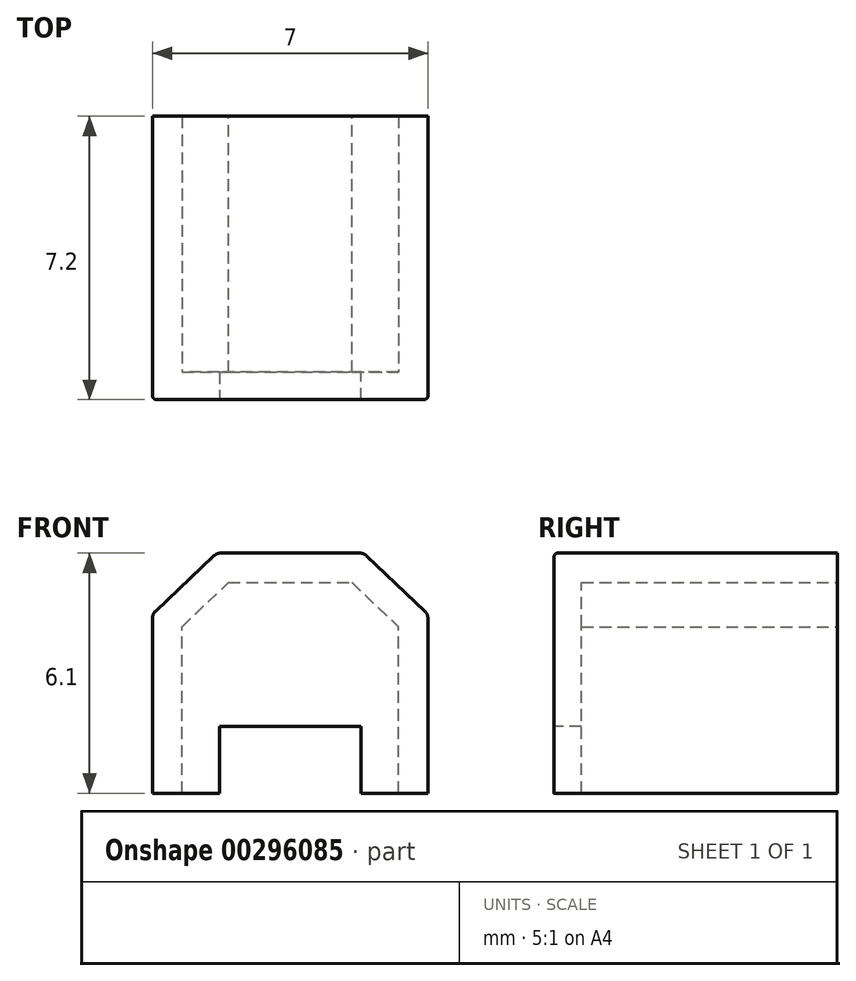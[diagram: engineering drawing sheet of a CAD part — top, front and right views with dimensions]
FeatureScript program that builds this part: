
annotation { "Feature Type Name" : "Feature", "Feature Type Description" : "" }
export const myFeature = defineFeature(function(context is Context, id is Id, definition is map)
    precondition{}
    {
        {
            var Q0;
            Q0=qCreatedBy(makeId("Front.planeOp"),FACE);
            var sketch = newSketch(context, id + "F0", { "sketchPlane" : qUnion([Q0])});
            skLineSegment(sketch, "E0.bottom", {"start": v(-3.5, 1.1) * mm, "end": v(3.5, 1.1) * mm});
            skLineSegment(sketch, "E0.left", {"start": v(-3.5, 1.1) * mm, "end": v(-3.5, 6.35) * mm});
            skLineSegment(sketch, "E0.right", {"start": v(3.5, 1.1) * mm, "end": v(3.5, 6.35) * mm});
            skPoint(sketch, "E1", {"position": v(0, 1.1) * mm});
            skLineSegment(sketch, "E2", {"start": v(-3.5, 6.35) * mm, "end": v(-1.87, 7.9) * mm});
            skLineSegment(sketch, "E3", {"start": v(-1.87, 7.9) * mm, "end": v(1.87, 7.9) * mm});
            skLineSegment(sketch, "E4", {"start": v(1.87, 7.9) * mm, "end": v(3.5, 6.35) * mm});
            skSolve(sketch);
        }
        {
            var Q0;
            Q0=makeQuery(id+"F0.imprint","IMPRINT",FACE,{"disambiguationData":[TD([[makeQuery(id+"F0.imprint","IMPRINT",EDGE,{"derivedFrom":sQuery(id+"F0.wireOp",EDGE,"E0.bottom")}),1.0]])]});
            extrude(context, id + "F1", {"entities" : qUnion([Q0]), "depth" : 7.2 * mm, "offsetDistance" : 25 * mm});
        }
        {
            var Q0;
            Q0=makeQuery(id+"F1.opExtrude","CAP_FACE",FACE,{"disambiguationData":[OSD([sQuery(id+"F0.wireOp",EDGE,"E0.bottom"),sQuery(id+"F0.wireOp",EDGE,"E0.left"),sQuery(id+"F0.wireOp",EDGE,"E0.right"),sQuery(id+"F0.wireOp",EDGE,"E2"),sQuery(id+"F0.wireOp",EDGE,"E3"),sQuery(id+"F0.wireOp",EDGE,"E4")])],"isStart":false});
            var sketch = newSketch(context, id + "F2", { "sketchPlane" : qUnion([Q0])});
            skLineSegment(sketch, "E5.0", {"start": v(-1.8, 1.1) * mm, "end": v(1.8, 1.1) * mm});
            skLineSegment(sketch, "E6", {"start": v(1.8, 1.1) * mm, "end": v(1.8, 3.5) * mm});
            skLineSegment(sketch, "E7", {"start": v(1.8, 3.5) * mm, "end": v(-1.8, 3.5) * mm});
            skLineSegment(sketch, "E8", {"start": v(-1.8, 3.5) * mm, "end": v(-1.8, 1.1) * mm});
            skPoint(sketch, "E9", {"position": v(0, 3.5) * mm});
            skPoint(sketch, "E10.orphan", {"position": v(-3.5, 1.1) * mm});
            skPoint(sketch, "E11.orphan", {"position": v(3.5, 1.1) * mm});
            skSolve(sketch);
        }
        {
            var Q0;
            Q0 = qSketchRegion(id + "F2", true);
            extrude(context, id + "F3", {"entities" : qUnion([Q0]), "operationType" : NewBodyOperationType.REMOVE, "endBound" : BoundingType.THROUGH_ALL, "oppositeDirection" : true, "depth" : 25 * mm, "offsetDistance" : 25 * mm});
        }
        {
            var Q0;
            Q0=makeQuery(id+"F1.opExtrude","CAP_FACE",FACE,{"disambiguationData":[OSD([sQuery(id+"F0.wireOp",EDGE,"E0.bottom"),sQuery(id+"F0.wireOp",EDGE,"E0.left"),sQuery(id+"F0.wireOp",EDGE,"E0.right"),sQuery(id+"F0.wireOp",EDGE,"E2"),sQuery(id+"F0.wireOp",EDGE,"E3"),sQuery(id+"F0.wireOp",EDGE,"E4")])],"isStart":true});
            var sketch = newSketch(context, id + "F4", { "sketchPlane" : qUnion([Q0])});
            skLineSegment(sketch, "E12.2", {"start": v(2.75, 1.1) * mm, "end": v(2.75, 6.03) * mm});
            skLineSegment(sketch, "E12.6", {"start": v(2.75, 6.03) * mm, "end": v(1.57, 7.15) * mm});
            skLineSegment(sketch, "E12.7", {"start": v(1.57, 7.15) * mm, "end": v(-1.57, 7.15) * mm});
            skLineSegment(sketch, "E12.8", {"start": v(-1.57, 7.15) * mm, "end": v(-2.75, 6.03) * mm});
            skLineSegment(sketch, "E12.9", {"start": v(-2.75, 1.1) * mm, "end": v(-2.75, 6.03) * mm});
            skLineSegment(sketch, "E13", {"start": v(-2.75, 1.1) * mm, "end": v(2.75, 1.1) * mm});
            skSolve(sketch);
        }
        {
            var Q0;
            Q0 = qSketchRegion(id + "F4", true);
            extrude(context, id + "F5", {"entities" : qUnion([Q0]), "operationType" : NewBodyOperationType.REMOVE, "oppositeDirection" : true, "depth" : 6.5 * mm, "offsetDistance" : 25 * mm});
        }
        {
            var Q0;
            Q0=makeQuery(id+"F1.opExtrude","CAP_FACE",FACE,{"disambiguationData":[OSD([sQuery(id+"F0.wireOp",EDGE,"E0.bottom"),sQuery(id+"F0.wireOp",EDGE,"E0.left"),sQuery(id+"F0.wireOp",EDGE,"E0.right"),sQuery(id+"F0.wireOp",EDGE,"E2"),sQuery(id+"F0.wireOp",EDGE,"E3"),sQuery(id+"F0.wireOp",EDGE,"E4")])],"isStart":false});
            var sketch = newSketch(context, id + "F6", { "sketchPlane" : qUnion([Q0])});
            skLineSegment(sketch, "E14.0", {"start": v(-3.5, 1.1) * mm, "end": v(-3.5, 1.8) * mm});
            skLineSegment(sketch, "E15.0", {"start": v(-3.5, 1.1) * mm, "end": v(3.5, 1.1) * mm});
            skPoint(sketch, "E16.orphan", {"position": v(-1.8, 1.1) * mm});
            skLineSegment(sketch, "E17.0", {"start": v(3.5, 1.1) * mm, "end": v(3.5, 1.8) * mm});
            skLineSegment(sketch, "E18", {"start": v(-3.5, 1.8) * mm, "end": v(3.5, 1.8) * mm});
            skPoint(sketch, "E19.orphan", {"position": v(-3.5, 6.35) * mm});
            skPoint(sketch, "E20.orphan", {"position": v(3.5, 6.35) * mm});
            skSolve(sketch);
        }
        {
            var Q0;
            Q0 = qSketchRegion(id + "F6", true);
            extrude(context, id + "F7", {"entities" : qUnion([Q0]), "operationType" : NewBodyOperationType.REMOVE, "endBound" : BoundingType.THROUGH_ALL, "oppositeDirection" : true, "depth" : 25 * mm, "offsetDistance" : 25 * mm});
        }
        {
            var Q0;
            Q0=makeQuery(id+"F1.opExtrude","SWEPT_EDGE",EDGE,{"disambiguationData":[OSD([sQuery(id+"F0.wireOp",EDGE,"E0.left"),sQuery(id+"F0.wireOp",EDGE,"E2")])]});
            var Q1;
            Q1=makeQuery(id+"F1.opExtrude","SWEPT_EDGE",EDGE,{"disambiguationData":[OSD([sQuery(id+"F0.wireOp",EDGE,"E2"),sQuery(id+"F0.wireOp",EDGE,"E3")])]});
            var Q2;
            Q2=makeQuery(id+"F1.opExtrude","SWEPT_EDGE",EDGE,{"disambiguationData":[OSD([sQuery(id+"F0.wireOp",EDGE,"E3"),sQuery(id+"F0.wireOp",EDGE,"E4")])]});
            var Q3;
            Q3=makeQuery(id+"F1.opExtrude","SWEPT_EDGE",EDGE,{"disambiguationData":[OSD([sQuery(id+"F0.wireOp",EDGE,"E0.right"),sQuery(id+"F0.wireOp",EDGE,"E4")])]});
            fillet(context, id + "F8", {"entities" : qUnion([Q0, Q1, Q2, Q3]), "radius" : 0.25 * mm, "tangentPropagation" : true, "allowEdgeOverflow" : false});
        }
        {
            var Q0;
            Q0=makeQuery(id+"F1.opExtrude","CAP_EDGE",EDGE,{"disambiguationData":[OSD([sQuery(id+"F0.wireOp",EDGE,"E0.left")])],"isStart":false});
            fillet(context, id + "F9", {"entities" : qUnion([Q0]), "radius" : 0.1 * mm, "tangentPropagation" : true, "allowEdgeOverflow" : false});
        }
    });
